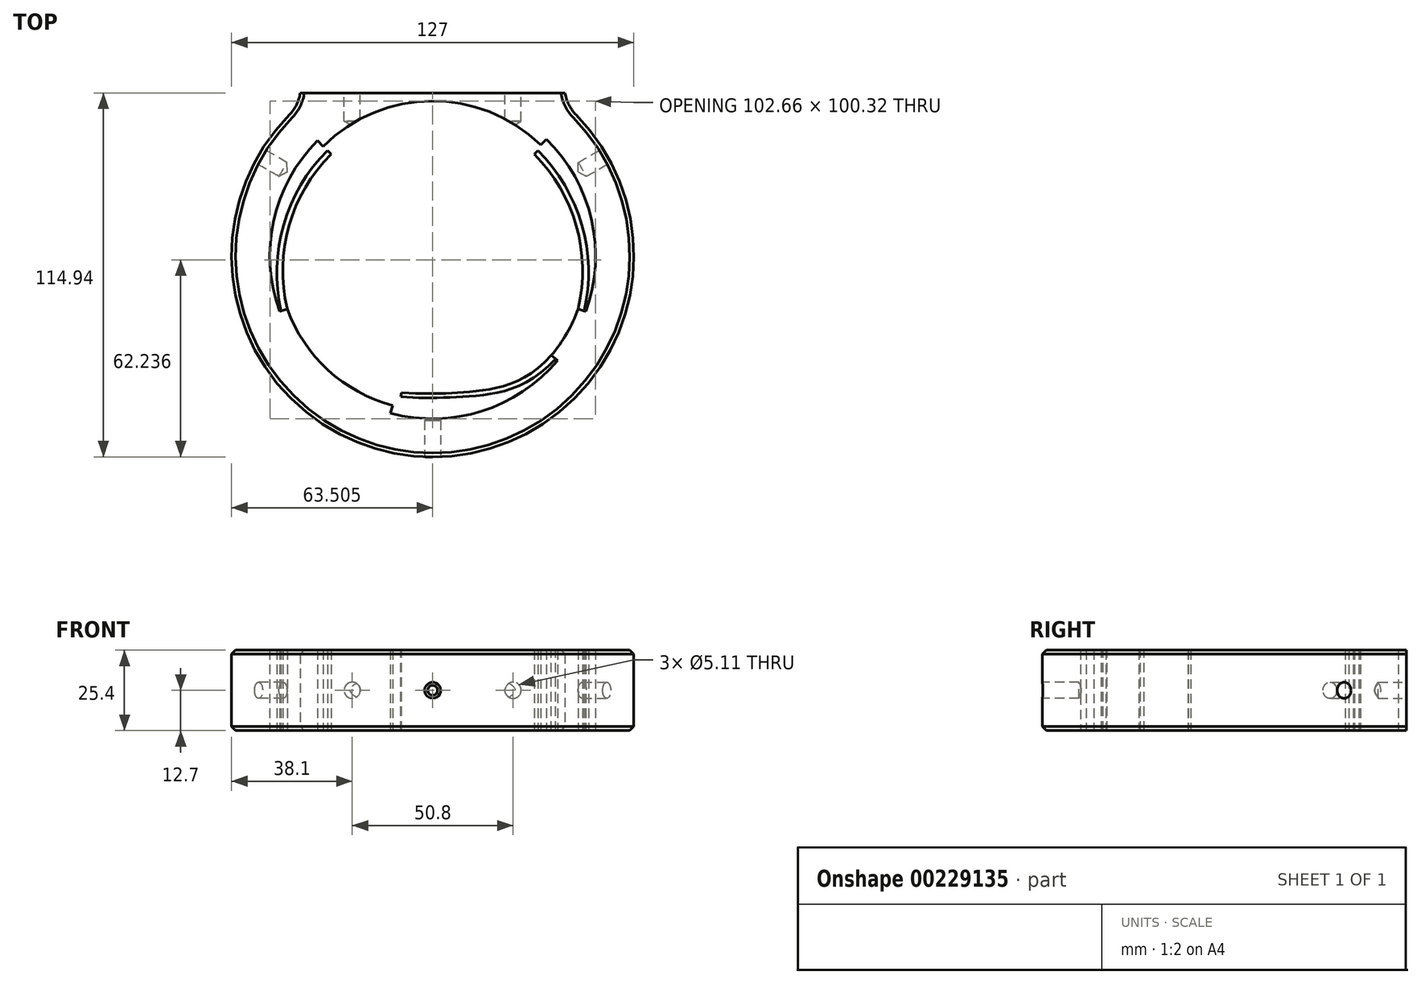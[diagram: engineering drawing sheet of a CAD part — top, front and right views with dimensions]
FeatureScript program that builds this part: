
annotation { "Feature Type Name" : "Feature", "Feature Type Description" : "" }
export const myFeature = defineFeature(function(context is Context, id is Id, definition is map)
    precondition{}
    {
        {
            var Q0;
            Q0=qCreatedBy(makeId("Top.planeOp"),FACE);
            var sketch = newSketch(context, id + "F0", { "sketchPlane" : qUnion([Q0])});
            skLineSegment(sketch, "E0", {"start": v(-41.8, 51.44) * mm, "end": v(41.8, 51.44) * mm});
            skArc(sketch, "E1", {"start": v(-45.3, 44.5) * mm, "mid": v(0, -63.5) * mm, "end": v(45.3, 44.5) * mm});
            skLineSegment(sketch, "E2", {"start": v(0, 0) * mm, "end": v(-53.03, 30.62) * mm, "construction": true});
            skArc(sketch, "E3.converted", {"start": v(-45.95, -16.72) * mm, "mid": v(-33.03, -36.05) * mm, "end": v(-12.65, -47.23) * mm});
            skLineSegment(sketch, "E4", {"start": v(0, 0) * mm, "end": v(64.7, 37.36) * mm, "construction": true});
            skArc(sketch, "E5", {"start": v(-36.37, 36.37) * mm, "mid": v(-50.22, 11.13) * mm, "end": v(-48.33, -17.6) * mm});
            skLineSegment(sketch, "E6", {"start": v(-45.95, -16.72) * mm, "end": v(-48.33, -17.6) * mm});
            skLineSegment(sketch, "E7", {"start": v(45.95, -16.72) * mm, "end": v(48.33, -17.6) * mm});
            skLineSegment(sketch, "E8", {"start": v(37.46, -31.43) * mm, "end": v(39.4, -33.06) * mm});
            skLineSegment(sketch, "E9", {"start": v(-12.65, -47.23) * mm, "end": v(-13.31, -49.68) * mm});
            skLineSegment(sketch, "E10", {"start": v(0, 0) * mm, "end": v(-0.5, 0.5) * mm});
            skLineSegment(sketch, "E11", {"start": v(34.08, 35.06) * mm, "end": v(35.87, 36.86) * mm});
            skLineSegment(sketch, "E12.trimOffspring", {"start": v(-34.57, 34.57) * mm, "end": v(-36.37, 36.37) * mm});
            skArc(sketch, "E13.trimOffspring", {"start": v(34.08, 35.06) * mm, "mid": v(-0.35, 48.9) * mm, "end": v(-34.57, 34.57) * mm});
            skArc(sketch, "E14.trimOffspring", {"start": v(37.46, -31.43) * mm, "mid": v(42.34, -24.45) * mm, "end": v(45.95, -16.72) * mm});
            skArc(sketch, "E15.trimOffspring", {"start": v(-13.31, -49.68) * mm, "mid": v(15.47, -49.05) * mm, "end": v(39.4, -33.06) * mm});
            skArc(sketch, "E16.trimOffspring", {"start": v(48.33, -17.6) * mm, "mid": v(50.14, 11.47) * mm, "end": v(35.87, 36.86) * mm});
            skLineSegment(sketch, "E17", {"start": v(-25.4, 37.69) * mm, "end": v(-25.4, 56.39) * mm, "construction": true});
            skLineSegment(sketch, "E18", {"start": v(25.4, 38.28) * mm, "end": v(25.4, 61.42) * mm, "construction": true});
            skPoint(sketch, "E19.visualSharp", {"position": v(-41.66, 47.93) * mm});
            skArc(sketch, "E19.filletArc", {"start": v(-45.3, 44.5) * mm, "mid": v(-43.01, 47.7) * mm, "end": v(-41.8, 51.44) * mm});
            skPoint(sketch, "E20.visualSharp", {"position": v(41.66, 47.93) * mm});
            skArc(sketch, "E20.filletArc", {"start": v(41.8, 51.44) * mm, "mid": v(43.01, 47.7) * mm, "end": v(45.3, 44.5) * mm});
            skSolve(sketch);
        }
        {
            var Q0;
            Q0 = qSketchRegion(id + "F0", true);
            extrude(context, id + "F1", {"entities" : qUnion([Q0]), "depth" : 25.4 * mm});
        }
        {
            var Q0;
            Q0=makeQuery(id+"F1.opExtrude","CAP_FACE",FACE,{"disambiguationData":[OSD([sQuery(id+"F0.wireOp",EDGE,"E0"),sQuery(id+"F0.wireOp",EDGE,"E1"),sQuery(id+"F0.wireOp",EDGE,"5337a609-aea6-4381-813d-a19e413b2fbd.trimOffspring"),sQuery(id+"F0.wireOp",EDGE,"bed2cc1c-05b2-4b47-84f1-faf123320268.trimOffspring"),sQuery(id+"F0.wireOp",EDGE,"E3.converted"),sQuery(id+"F0.wireOp",EDGE,"E5"),sQuery(id+"F0.wireOp",EDGE,"E6"),sQuery(id+"F0.wireOp",EDGE,"E7"),sQuery(id+"F0.wireOp",EDGE,"E8"),sQuery(id+"F0.wireOp",EDGE,"E9"),sQuery(id+"F0.wireOp",EDGE,"E11"),sQuery(id+"F0.wireOp",EDGE,"E12.trimOffspring"),sQuery(id+"F0.wireOp",EDGE,"E13.trimOffspring"),sQuery(id+"F0.wireOp",EDGE,"E14.trimOffspring"),sQuery(id+"F0.wireOp",EDGE,"E15.trimOffspring"),sQuery(id+"F0.wireOp",EDGE,"E16.trimOffspring"),sQuery(id+"F0.wireOp",EDGE,"E19.filletArc"),sQuery(id+"F0.wireOp",EDGE,"E20.filletArc")])],"isStart":false});
            var sketch = newSketch(context, id + "F2", { "sketchPlane" : qUnion([Q0])});
            skCircle(sketch, "E21", {"center": v(0, 0.64) * mm, "radius": 44.45 * mm, "construction": true});
            skSolve(sketch);
        }
        {
            var Q0;
            Q0=makeQuery(id+"F2.imprint","IMPRINT",FACE,{"disambiguationData":[TD([[makeQuery(id+"F2.imprint","IMPRINT",EDGE,{"derivedFrom":makeQuery(id+"F1.opExtrude","CAP_EDGE",EDGE,{"disambiguationData":[OSD([sQuery(id+"F0.wireOp",EDGE,"E0")])],"isStart":false})}),-1.0]])]});
            var sketch = newSketch(context, id + "F3", { "sketchPlane" : qUnion([Q0])});
            skLineSegment(sketch, "E22", {"start": v(-9.77, -43.15) * mm, "end": v(-10.05, -44.42) * mm});
            skLineSegment(sketch, "E23", {"start": v(37.46, -31.43) * mm, "end": v(38.82, -32.57) * mm});
            skFitSpline(sketch, "E24", {"points": [v(37.46, -31.43) * mm, v(10.62, -43) * mm, v(-9.77, -43.15) * mm], "startDerivative": vector(-46.74, -53.38) * mm, "endDerivative": vector(-54.52, 3.6) * mm});
            skFitSpline(sketch, "E25", {"points": [v(38.82, -32.57) * mm, v(9.92, -44.44) * mm, v(-10.05, -44.42) * mm], "startDerivative": vector(-53.2, -56.57) * mm, "endDerivative": vector(-43.49, 4.58) * mm});
            skSolve(sketch);
        }
        {
            var Q0;
            Q0 = qSketchRegion(id + "F3", true);
            extrude(context, id + "F4", {"entities" : qUnion([Q0]), "oppositeDirection" : true, "depth" : 25.4 * mm});
        }
        {
            var Q0;
            Q0=makeQuery(id+"F1.opExtrude","CAP_FACE",FACE,{"disambiguationData":[OSD([sQuery(id+"F0.wireOp",EDGE,"E0"),sQuery(id+"F0.wireOp",EDGE,"E1"),sQuery(id+"F0.wireOp",EDGE,"5337a609-aea6-4381-813d-a19e413b2fbd.trimOffspring"),sQuery(id+"F0.wireOp",EDGE,"bed2cc1c-05b2-4b47-84f1-faf123320268.trimOffspring"),sQuery(id+"F0.wireOp",EDGE,"E3.converted"),sQuery(id+"F0.wireOp",EDGE,"E5"),sQuery(id+"F0.wireOp",EDGE,"E6"),sQuery(id+"F0.wireOp",EDGE,"E7"),sQuery(id+"F0.wireOp",EDGE,"E8"),sQuery(id+"F0.wireOp",EDGE,"E9"),sQuery(id+"F0.wireOp",EDGE,"E11"),sQuery(id+"F0.wireOp",EDGE,"E12.trimOffspring"),sQuery(id+"F0.wireOp",EDGE,"E13.trimOffspring"),sQuery(id+"F0.wireOp",EDGE,"E14.trimOffspring"),sQuery(id+"F0.wireOp",EDGE,"E15.trimOffspring"),sQuery(id+"F0.wireOp",EDGE,"E16.trimOffspring"),sQuery(id+"F0.wireOp",EDGE,"E19.filletArc"),sQuery(id+"F0.wireOp",EDGE,"E20.filletArc")])],"isStart":true});
            var sketch = newSketch(context, id + "F5", { "sketchPlane" : qUnion([Q0])});
            skLineSegment(sketch, "E26", {"start": v(-33.23, -33.23) * mm, "end": v(-32.09, -32.09) * mm, "construction": true});
            skArc(sketch, "E27", {"start": v(-45.95, 16.72) * mm, "mid": v(-45.36, -9.48) * mm, "end": v(-32.09, -32.09) * mm});
            skArc(sketch, "E28", {"start": v(-47.88, 17.43) * mm, "mid": v(-47.07, -9.79) * mm, "end": v(-33.23, -33.23) * mm});
            skLineSegment(sketch, "E29", {"start": v(-47.88, 17.43) * mm, "end": v(-45.95, 16.72) * mm});
            skLineSegment(sketch, "E30", {"start": v(-32.09, -32.09) * mm, "end": v(-33.23, -33.23) * mm});
            skLineSegment(sketch, "E31.trimOffspring", {"start": v(0, 0) * mm, "end": v(21.6, 21.6) * mm, "construction": true});
            skSolve(sketch);
        }
        {
            var Q0;
            Q0 = qSketchRegion(id + "F5", true);
            extrude(context, id + "F6", {"entities" : qUnion([Q0]), "oppositeDirection" : true, "depth" : 25.4 * mm});
        }
        {
            var Q0;
            Q0=qCreatedBy(makeId("Front.planeOp"),FACE);
            var sketch = newSketch(context, id + "F7", { "sketchPlane" : qUnion([Q0])});
            skLineSegment(sketch, "E32", {"start": v(43.7, 12.7) * mm, "end": v(-18.01, 12.7) * mm, "construction": true});
            skLineSegment(sketch, "E33", {"start": v(38.82, 25.4) * mm, "end": v(-9.77, 25.4) * mm});
            skLineSegment(sketch, "E34", {"start": v(38.82, 25.4) * mm, "end": v(-9.77, 15.24) * mm});
            skLineSegment(sketch, "E35", {"start": v(-9.77, 15.24) * mm, "end": v(-9.77, 25.4) * mm});
            skSolve(sketch);
        }
        {
            var Q0;
            Q0=qCreatedBy(makeId("Top.planeOp"),FACE);
            cPlane(context, id + "F8", {"entities" : qUnion([Q0]), "cplaneType" : CPlaneType.OFFSET, "offset" : 12.7 * mm, "width" : 152.4 * mm, "height" : 152.4 * mm});
        }
        {
            var Q0;
            Q0=qCreatedBy(makeId("Right.planeOp"),FACE);
            var sketch = newSketch(context, id + "F9", { "sketchPlane" : qUnion([Q0])});
            skLineSegment(sketch, "E36", {"start": v(-17.43, 25.4) * mm, "end": v(33.23, 15.24) * mm});
            skLineSegment(sketch, "E37", {"start": v(33.23, 15.24) * mm, "end": v(33.23, 25.4) * mm});
            skLineSegment(sketch, "E38", {"start": v(33.23, 25.4) * mm, "end": v(-17.43, 25.4) * mm});
            skSolve(sketch);
        }
        {
            var Q0;
            Q0=makeQuery(id+"F6.opExtrude","SWEPT_BODY",BODY,{"disambiguationData":[OSD([sQuery(id+"F5.wireOp",EDGE,"E27"),sQuery(id+"F5.wireOp",EDGE,"E28"),sQuery(id+"F5.wireOp",EDGE,"E29"),sQuery(id+"F5.wireOp",EDGE,"E30")])]});
            var Q1;
            Q1=qCreatedBy(makeId("Right.planeOp"),FACE);
            mirror(context, id + "F10", {"entities" : qUnion([Q0]), "mirrorPlane" : qUnion([Q1])});
        }
        {
            var Q0;
            Q0=qCreatedBy(id+"F8.planeOp",FACE);
            var sketch = newSketch(context, id + "F11", { "sketchPlane" : qUnion([Q0])});
            skLineSegment(sketch, "E39", {"start": v(-30.95, -63.5) * mm, "end": v(39, -63.5) * mm, "construction": true});
            skLineSegment(sketch, "E40", {"start": v(-54.96, 31.8) * mm, "end": v(-69.68, 6.3) * mm, "construction": true});
            skLineSegment(sketch, "E41", {"start": v(50.35, 39.78) * mm, "end": v(67.11, 10.76) * mm, "construction": true});
            skSolve(sketch);
        }
        {
            var Q0;
            Q0=sQuery(id+"F11.wireOp",EDGE,"E39");
            var Q1;
            Q1=qCreatedBy(id+"F8.planeOp",FACE);
            cPlane(context, id + "F12", {"entities" : qUnion([Q0, Q1]), "cplaneType" : CPlaneType.LINE_ANGLE, "offset" : 25.4 * mm, "angle" : 90 * degree, "width" : 152.4 * mm, "height" : 152.4 * mm});
        }
        {
            var Q0;
            Q0=sQuery(id+"F11.wireOp",EDGE,"E40");
            cPlane(context, id + "F13", {"entities" : qUnion([Q0]), "cplaneType" : CPlaneType.LINE_ANGLE, "offset" : 25.4 * mm, "angle" : 90 * degree, "width" : 152.4 * mm, "height" : 152.4 * mm});
        }
        {
            var Q0;
            Q0=sQuery(id+"F11.wireOp",EDGE,"E41");
            cPlane(context, id + "F14", {"entities" : qUnion([Q0]), "cplaneType" : CPlaneType.LINE_ANGLE, "offset" : 25.4 * mm, "angle" : 90 * degree, "width" : 152.4 * mm, "height" : 152.4 * mm});
        }
        {
            var Q0;
            Q0=qCreatedBy(id+"F13.planeOp",FACE);
            var sketch = newSketch(context, id + "F15", { "sketchPlane" : qUnion([Q0])});
            skPoint(sketch, "E42", {"position": v(0, 12.7) * mm});
            skSolve(sketch);
        }
        {
            var Q0;
            Q0=sQuery(id+"F15.wireOp",VERTEX,"E42");
            var Q1;
            Q1=makeQuery(id+"F1.opExtrude","SWEPT_BODY",BODY,{"disambiguationData":[OSD([sQuery(id+"F0.wireOp",EDGE,"E0"),sQuery(id+"F0.wireOp",EDGE,"E1"),sQuery(id+"F0.wireOp",EDGE,"5337a609-aea6-4381-813d-a19e413b2fbd.trimOffspring"),sQuery(id+"F0.wireOp",EDGE,"bed2cc1c-05b2-4b47-84f1-faf123320268.trimOffspring"),sQuery(id+"F0.wireOp",EDGE,"E3.converted"),sQuery(id+"F0.wireOp",EDGE,"E5"),sQuery(id+"F0.wireOp",EDGE,"E6"),sQuery(id+"F0.wireOp",EDGE,"E7"),sQuery(id+"F0.wireOp",EDGE,"E8"),sQuery(id+"F0.wireOp",EDGE,"E9"),sQuery(id+"F0.wireOp",EDGE,"E11"),sQuery(id+"F0.wireOp",EDGE,"E12.trimOffspring"),sQuery(id+"F0.wireOp",EDGE,"E13.trimOffspring"),sQuery(id+"F0.wireOp",EDGE,"E14.trimOffspring"),sQuery(id+"F0.wireOp",EDGE,"E15.trimOffspring"),sQuery(id+"F0.wireOp",EDGE,"E16.trimOffspring"),sQuery(id+"F0.wireOp",EDGE,"E19.filletArc"),sQuery(id+"F0.wireOp",EDGE,"E20.filletArc")])]});
            hole(context, id + "F16", {"style" : HoleStyle.SIMPLE, "endStyle" : HoleEndStyle.BLIND, "oppositeDirection" : true, "standardTappedOrClearance" : lookupTablePath({ "standard" : "ANSI", "engagement" : "75%", "pitch" : "20 tpi", "size" : "1/4", "type" : "Tapped" }), "standardBlindInLast" : lookupTablePath({ "standard" : "ANSI", "engagement" : "75%", "pitch" : "20 tpi", "size" : "1/4", "type" : "Tapped" }), "holeDiameter" : 5.1 * mm, "holeDepth" : 8.9 * mm, "locations" : qUnion([Q0]), "scope" : qUnion([Q1]), "majorDiameter" : 6.35 * mm});
        }
        {
            var Q0;
            Q0=qCreatedBy(id+"F12.planeOp",FACE);
            var sketch = newSketch(context, id + "F17", { "sketchPlane" : qUnion([Q0])});
            skPoint(sketch, "E43", {"position": v(0, 12.7) * mm});
            skSolve(sketch);
        }
        {
            var Q0;
            Q0=sQuery(id+"F17.wireOp",VERTEX,"E43");
            var Q1;
            Q1=makeQuery(id+"F1.opExtrude","SWEPT_BODY",BODY,{"disambiguationData":[OSD([sQuery(id+"F0.wireOp",EDGE,"E0"),sQuery(id+"F0.wireOp",EDGE,"E1"),sQuery(id+"F0.wireOp",EDGE,"5337a609-aea6-4381-813d-a19e413b2fbd.trimOffspring"),sQuery(id+"F0.wireOp",EDGE,"bed2cc1c-05b2-4b47-84f1-faf123320268.trimOffspring"),sQuery(id+"F0.wireOp",EDGE,"E3.converted"),sQuery(id+"F0.wireOp",EDGE,"E5"),sQuery(id+"F0.wireOp",EDGE,"E6"),sQuery(id+"F0.wireOp",EDGE,"E7"),sQuery(id+"F0.wireOp",EDGE,"E8"),sQuery(id+"F0.wireOp",EDGE,"E9"),sQuery(id+"F0.wireOp",EDGE,"E11"),sQuery(id+"F0.wireOp",EDGE,"E12.trimOffspring"),sQuery(id+"F0.wireOp",EDGE,"E13.trimOffspring"),sQuery(id+"F0.wireOp",EDGE,"E14.trimOffspring"),sQuery(id+"F0.wireOp",EDGE,"E15.trimOffspring"),sQuery(id+"F0.wireOp",EDGE,"E16.trimOffspring"),sQuery(id+"F0.wireOp",EDGE,"E19.filletArc"),sQuery(id+"F0.wireOp",EDGE,"E20.filletArc")])]});
            hole(context, id + "F18", {"style" : HoleStyle.SIMPLE, "endStyle" : HoleEndStyle.BLIND, "oppositeDirection" : true, "standardTappedOrClearance" : lookupTablePath({ "standard" : "ANSI", "engagement" : "75%", "pitch" : "20 tpi", "size" : "1/4", "type" : "Tapped" }), "standardBlindInLast" : lookupTablePath({ "standard" : "ANSI", "engagement" : "75%", "pitch" : "20 tpi", "size" : "1/4", "type" : "Tapped" }), "holeDiameter" : 5.1 * mm, "holeDepth" : 11.43 * mm, "locations" : qUnion([Q0]), "scope" : qUnion([Q1]), "majorDiameter" : 6.35 * mm});
        }
        {
            var Q0;
            Q0=qCreatedBy(id+"F14.planeOp",FACE);
            var sketch = newSketch(context, id + "F19", { "sketchPlane" : qUnion([Q0])});
            skPoint(sketch, "E44", {"position": v(0, 12.7) * mm});
            skSolve(sketch);
        }
        {
            var Q0;
            Q0=sQuery(id+"F19.wireOp",VERTEX,"E44");
            var Q1;
            Q1=makeQuery(id+"F1.opExtrude","SWEPT_BODY",BODY,{"disambiguationData":[OSD([sQuery(id+"F0.wireOp",EDGE,"E0"),sQuery(id+"F0.wireOp",EDGE,"E1"),sQuery(id+"F0.wireOp",EDGE,"5337a609-aea6-4381-813d-a19e413b2fbd.trimOffspring"),sQuery(id+"F0.wireOp",EDGE,"bed2cc1c-05b2-4b47-84f1-faf123320268.trimOffspring"),sQuery(id+"F0.wireOp",EDGE,"E3.converted"),sQuery(id+"F0.wireOp",EDGE,"E5"),sQuery(id+"F0.wireOp",EDGE,"E6"),sQuery(id+"F0.wireOp",EDGE,"E7"),sQuery(id+"F0.wireOp",EDGE,"E8"),sQuery(id+"F0.wireOp",EDGE,"E9"),sQuery(id+"F0.wireOp",EDGE,"E11"),sQuery(id+"F0.wireOp",EDGE,"E12.trimOffspring"),sQuery(id+"F0.wireOp",EDGE,"E13.trimOffspring"),sQuery(id+"F0.wireOp",EDGE,"E14.trimOffspring"),sQuery(id+"F0.wireOp",EDGE,"E15.trimOffspring"),sQuery(id+"F0.wireOp",EDGE,"E16.trimOffspring"),sQuery(id+"F0.wireOp",EDGE,"E19.filletArc"),sQuery(id+"F0.wireOp",EDGE,"E20.filletArc")])]});
            hole(context, id + "F20", {"style" : HoleStyle.SIMPLE, "endStyle" : HoleEndStyle.BLIND, "standardTappedOrClearance" : lookupTablePath({ "standard" : "ANSI", "engagement" : "75%", "pitch" : "20 tpi", "size" : "1/4", "type" : "Tapped" }), "standardBlindInLast" : lookupTablePath({ "standard" : "ANSI", "engagement" : "75%", "pitch" : "20 tpi", "size" : "1/4", "type" : "Tapped" }), "holeDiameter" : 5.1 * mm, "holeDepth" : 8.9 * mm, "locations" : qUnion([Q0]), "scope" : qUnion([Q1]), "majorDiameter" : 6.35 * mm});
        }
        {
            var Q0;
            Q0=sQuery(id+"F0.wireOp",EDGE,"E0");
            cPlane(context, id + "F21", {"entities" : qUnion([Q0]), "cplaneType" : CPlaneType.LINE_ANGLE, "offset" : 25.4 * mm, "angle" : 0 * degree, "width" : 152.4 * mm, "height" : 152.4 * mm});
        }
        {
            var Q0;
            Q0=qCreatedBy(id+"F21.planeOp",FACE);
            var sketch = newSketch(context, id + "F22", { "sketchPlane" : qUnion([Q0])});
            skLineSegment(sketch, "E45", {"start": v(-88.08, 12.7) * mm, "end": v(108.95, 12.7) * mm, "construction": true});
            skPoint(sketch, "E46", {"position": v(-25.4, 12.7) * mm});
            skPoint(sketch, "E47", {"position": v(25.4, 12.7) * mm});
            skSolve(sketch);
        }
        {
            var Q0;
            Q0=sQuery(id+"F22.wireOp",VERTEX,"E46");
            var Q1;
            Q1=sQuery(id+"F22.wireOp",VERTEX,"E47");
            var Q2;
            Q2=makeQuery(id+"F1.opExtrude","SWEPT_BODY",BODY,{"disambiguationData":[OSD([sQuery(id+"F0.wireOp",EDGE,"E0"),sQuery(id+"F0.wireOp",EDGE,"E1"),sQuery(id+"F0.wireOp",EDGE,"5337a609-aea6-4381-813d-a19e413b2fbd.trimOffspring"),sQuery(id+"F0.wireOp",EDGE,"bed2cc1c-05b2-4b47-84f1-faf123320268.trimOffspring"),sQuery(id+"F0.wireOp",EDGE,"E3.converted"),sQuery(id+"F0.wireOp",EDGE,"E5"),sQuery(id+"F0.wireOp",EDGE,"E6"),sQuery(id+"F0.wireOp",EDGE,"E7"),sQuery(id+"F0.wireOp",EDGE,"E8"),sQuery(id+"F0.wireOp",EDGE,"E9"),sQuery(id+"F0.wireOp",EDGE,"E11"),sQuery(id+"F0.wireOp",EDGE,"E12.trimOffspring"),sQuery(id+"F0.wireOp",EDGE,"E13.trimOffspring"),sQuery(id+"F0.wireOp",EDGE,"E14.trimOffspring"),sQuery(id+"F0.wireOp",EDGE,"E15.trimOffspring"),sQuery(id+"F0.wireOp",EDGE,"E16.trimOffspring"),sQuery(id+"F0.wireOp",EDGE,"E19.filletArc"),sQuery(id+"F0.wireOp",EDGE,"E20.filletArc")])]});
            hole(context, id + "F23", {"style" : HoleStyle.SIMPLE, "endStyle" : HoleEndStyle.BLIND, "standardTappedOrClearance" : lookupTablePath({ "standard" : "ANSI", "engagement" : "75%", "pitch" : "20 tpi", "size" : "1/4", "type" : "Tapped" }), "standardBlindInLast" : lookupTablePath({ "standard" : "ANSI", "engagement" : "75%", "pitch" : "20 tpi", "size" : "1/4", "type" : "Tapped" }), "holeDiameter" : 5.1 * mm, "holeDepth" : 8.9 * mm, "locations" : qUnion([Q0, Q1]), "scope" : qUnion([Q2]), "majorDiameter" : 6.35 * mm});
        }
        {
            var Q0;
            Q0=makeQuery(id+"F1.opExtrude","CAP_EDGE",EDGE,{"disambiguationData":[OSD([sQuery(id+"F0.wireOp",EDGE,"E1")])],"isStart":false});
            var Q1;
            Q1=makeQuery(id+"F1.opExtrude","CAP_EDGE",EDGE,{"disambiguationData":[OSD([sQuery(id+"F0.wireOp",EDGE,"E1")])],"isStart":true});
            chamfer(context, id + "F24", {"entities" : qUnion([Q0, Q1]), "width" : 1.27 * mm, "tangentPropagation" : true});
        }
    });
